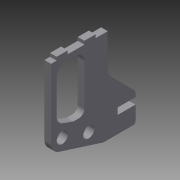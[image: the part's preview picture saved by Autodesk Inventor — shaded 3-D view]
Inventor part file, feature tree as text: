
AUTODESK INVENTOR PART (.ipt)
format: ipt  version: 2015 (Build 190159000, 159)  size: 166,400 bytes
history: native  units: mm
features: extrude x1, sketch x1
ambient origin geometry x8: Origin, YZ Plane, XZ Plane, XY Plane, X Axis, Y Axis, Z Axis, Center Point
bodies: Body1 (feature_tree)
feature tree (2):
  extrude  "Extrusion10"  Depth=10.0mm
  sketch  "Sketch1"  dims[d5=50.0mm d6=66.5mm d10=5.0mm d17=10.0mm d18=3.0mm d20=10.0mm d21=3.0mm d22=5.0mm d23=15.0mm d24=3.0mm d25=3.0mm d75=90.0deg d80=75.0mm d129=64.0mm d130=16.0mm d131=60.0mm d139=5.8mm d148=5.0mm d149=5.0mm d152=8.0mm d162=10.0mm d164=27.925268mm d167=55.0mm d169=5.0mm d170=5.0mm d171=8.0mm d173=10.0mm d174=6.0mm d175=0.0mm d184=5.0mm d185=30.0mm d186=135.0deg d187=10.0mm d188=5.0mm d189=25.0mm d190=15.0mm d191=25.0mm d192=2.0mm]
